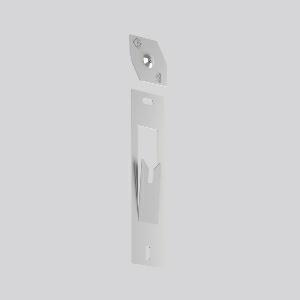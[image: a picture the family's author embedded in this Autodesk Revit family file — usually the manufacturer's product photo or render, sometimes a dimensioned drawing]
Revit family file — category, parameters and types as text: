
# Revit family: linedo_wand_adapter_982814_000_9ddb
name_source: partatom
category: Lighting Fixtures
units: mm (PartAtom-declared; Revit-internal decimal feet)

## family parameters
Cut with Voids When Loaded = No
Host = Face
Light Source = No
Part Type = Normal
Room Calculation Point = No
Round Connector Dimension = Use Diameter
Shared = No

## types (1)
- LINEDO Wand Adapter
    Apparent Load = 0 VA
    Default Elevation = 1800 mm
    Description = Wall mounting made of galvanised sheet steel. For vertical installation of LINEDO luminaire modules. 2 wall suspensions are required per luminaire module (max. 1 x 8 units). With this accessory, the protection type of the luminaire module can be reduced to IP 20.
Colour: unpainted
Length: 200 mm
Width: 53 mm
Height: 9 mm
Weight: 121 g
Type of Installation: Wall (surface)
    Height = 9 mm  [stored 0.0295276 ft]
    Lamp = 0 x
    Length = 200 mm  [stored 0.656168 ft]
    Luminous efficacy = 0 lm/W
    Manufacturer = RZB
    ModVariant = No
    Model = 982814.000
    Mounting Place = Ceiling
    Mounting Type = Surface mounted
    Number of Poles = 1
    OnlyDefault = Yes
    Power Factor = 1
    Product Name = LINEDO Wand Adapter
    Product group = Surface mounted continuous line luminaire system
    ProductGroupID = 310
    Protection Class = Protection class
    Protection Degree = Degree of protection
    RLX_Detail_Level = 1
    RLX_Emergency_Light_Flux = 0 lm
    RLX_Emergency_Type = 0
    RLX_Emergency_Type_DB = No
    RlxData = <blob elided: 10249 chars, md5=955dd2bd>
    Standby Power = 0 W
    System Light Flux = 0 lm
    System Power = 0 W
    Type Comments = Product without accessories
    Type Image = 982814.000.jpg
    URL = http://relux.com
    VarID = ---
    Voltage = 0 V
    Weight = 0.00 kg
    Width = 53 mm

note: [stored X ft] marks values corroborated as IEEE doubles in the binary element streams (Revit-internal decimal feet)

## geometry (parser evidence)
native form markers: Sweep x10
no freeform markers — native parametric forms only
